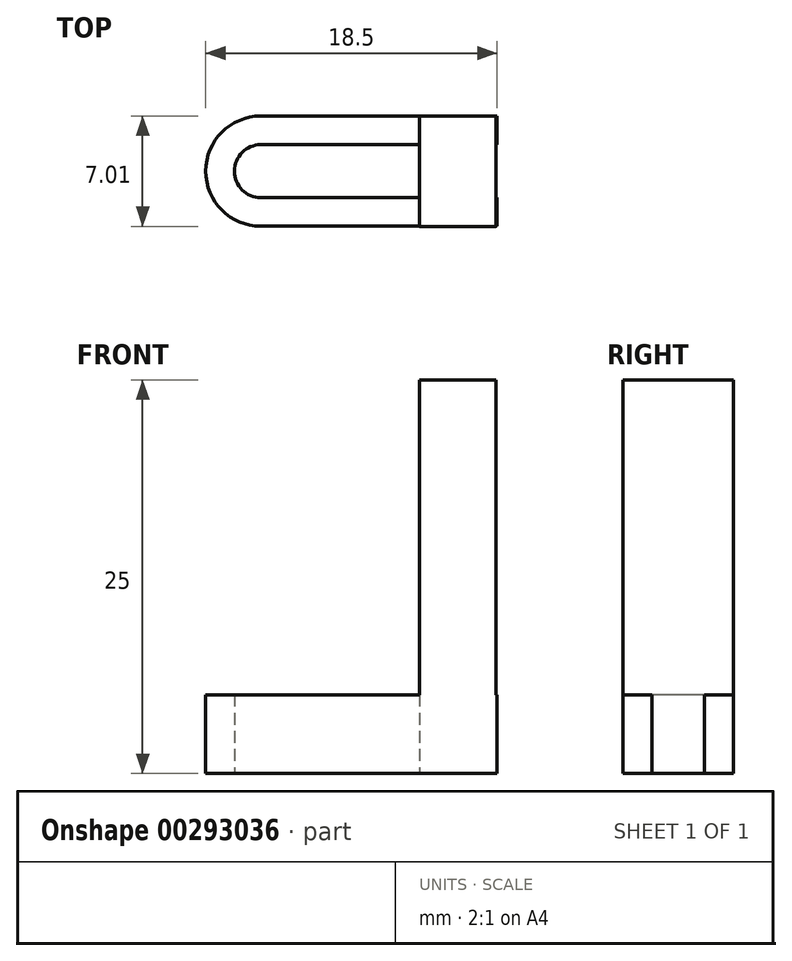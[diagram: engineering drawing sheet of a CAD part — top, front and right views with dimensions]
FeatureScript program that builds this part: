
annotation { "Feature Type Name" : "Feature", "Feature Type Description" : "" }
export const myFeature = defineFeature(function(context is Context, id is Id, definition is map)
    precondition{}
    {
        {
            var Q0;
            Q0=qCreatedBy(makeId("Top.planeOp"),FACE);
            var sketch = newSketch(context, id + "F0", { "sketchPlane" : qUnion([Q0])});
            skLineSegment(sketch, "E0.bottom", {"start": v(0, 0) * mm, "end": v(15, 0) * mm});
            skLineSegment(sketch, "E0.top", {"start": v(0, -7) * mm, "end": v(15, -7) * mm});
            skLineSegment(sketch, "E0.left", {"start": v(0, 0) * mm, "end": v(0, -7) * mm, "construction": true});
            skLineSegment(sketch, "E0.right", {"start": v(15, 0) * mm, "end": v(15, -7) * mm});
            skArc(sketch, "E1", {"start": v(0, 0) * mm, "mid": v(-3.5, -3.5) * mm, "end": v(0, -7) * mm});
            skLineSegment(sketch, "E2.0", {"start": v(0, -5.18) * mm, "end": v(15, -5.18) * mm});
            skArc(sketch, "E2.1", {"start": v(0, -1.82) * mm, "mid": v(-1.68, -3.5) * mm, "end": v(0, -5.18) * mm});
            skLineSegment(sketch, "E2.2", {"start": v(0, -1.82) * mm, "end": v(15, -1.82) * mm});
            skArc(sketch, "E3", {"start": v(9.77, -5.18) * mm, "mid": v(11.2, -3.51) * mm, "end": v(9.8, -1.82) * mm});
            skSolve(sketch);
        }
        {
            var Q0;
            {var subQ4=sQuery(id+"F0.wireOp",EDGE,"E0.bottom");Q0=makeQuery(id+"F0.imprint","IMPRINT",FACE,{"disambiguationData":[TD([[makeQuery(id+"F0.imprint","IMPRINT",EDGE,{"derivedFrom":subQ4}),-1.0]])]});}
            extrude(context, id + "F1", {"entities" : qUnion([Q0]), "depth" : 5 * mm});
        }
        {
            var Q0;
            Q0=qCreatedBy(makeId("Top.planeOp"),FACE);
            var sketch = newSketch(context, id + "F2", { "sketchPlane" : qUnion([Q0])});
            skLineSegment(sketch, "E4.bottom", {"start": v(14.95, 0) * mm, "end": v(10.08, 0) * mm});
            skLineSegment(sketch, "E4.top", {"start": v(14.95, -7) * mm, "end": v(10.08, -7) * mm});
            skLineSegment(sketch, "E4.left", {"start": v(14.95, 0) * mm, "end": v(14.95, -7) * mm});
            skLineSegment(sketch, "E4.right", {"start": v(10.08, 0) * mm, "end": v(10.08, -7) * mm});
            skSolve(sketch);
        }
        {
            var Q0;
            Q0=makeQuery(id+"F2.imprint","IMPRINT",FACE,{"disambiguationData":[TD([[makeQuery(id+"F2.imprint","IMPRINT",EDGE,{"derivedFrom":sQuery(id+"F2.wireOp",EDGE,"E4.bottom")}),1.0]])]});
            extrude(context, id + "F3", {"entities" : qUnion([Q0]), "operationType" : NewBodyOperationType.ADD, "depth" : 25 * mm});
        }
    });
